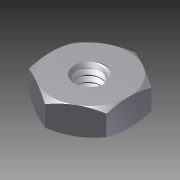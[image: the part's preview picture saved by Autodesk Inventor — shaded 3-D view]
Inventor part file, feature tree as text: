
AUTODESK INVENTOR PART (.ipt)
format: ipt  version: 2015 (Build 190159000, 159)  size: 314,368 bytes
history: native  units: in
note: dims shown in document units (in); Inventor stores cm internally (conversion verified against a paired STEP export)
features: mirror x1, other x1, imported_body x1
ambient origin geometry x8: Origin, YZ Plane, XZ Plane, XY Plane, X Axis, Y Axis, Z Axis, Center Point
bodies: Body1 (feature_tree)
feature tree (3):
  mirror  "Mirror1"
  other  "90480A0061"
  imported_body  "Base1"
